# Revit family: Shower-Shower_Door-KOHLER-Levity-K-706016.rfa_
name_source: partatom
category: Specialty Equipment
units: mm (PartAtom-declared; Revit-internal decimal feet)

## family parameters
Cut with Voids When Loaded = No
Host = Face
OmniClass Number = 23.31.17.17
OmniClass Title = Shower Enclosures
Part Type = Normal
Room Calculation Point = No
Round Connector Dimension = Use Diameter
Shared = No

## types (4) — shared parameters
ADA Compliant = No
Assembly Code = C1030200
Date Modified = 07/13/2023
Default Elevation = 4"
Description = Sliding Shower Door, 74 Inch H x 44-5/8 - 47-5/8 Inch W, With 3/8 Inch Thick Crystal Clear Glass And Square Towel Bar
Hardware Included = Yes
Height = 73 9/16"
Length = 7 3/4"
Manufacturer = Kohler Co.
Master Format 2014 = 10 28 19.16
Master Format 2014 Name = Shower Doors
Material = Premium Metal Construction
Product Documentation Link = https://www.us.kohler.com
Product Name = Levity
Product Page URL = http://www.us.kohler.com
URL = https://www.us.kohler.com
WaterSense Certified = No

## per-type parameters (varying)
| type | Finish | Model | Secondary Finish | Towel Bar Finish | Type |
| ABV-Anodized Brushed Bronze | Kohler-Metal-ABV-Anodized_Brushed_Bronze | K-706016-L-ABV | Kohler-Plastic-BV-Brushed_Bronze | Kohler-Metal-BV-Brushed_Bronze | 1 |
| NX-Brushed Nickel | Kohler-Metal-NX-Brushed_Nickel | K-706016-L-NX | KOHLER-Plastic-BN-Vibrant_Brushed_Nickel | Kohler-Metal-BN-Vibrant_Brushed_Nickel | 2 |
| SHP-Bright Polished Silver | Kohler-Metal-SHP-Bright_Polished_Silver | K-706016-L-SHP | Kohler-Plastic-CP-Polished_Chrome | Kohler-Metal-CP-Polished_Chrome | 3 |
| SH-Bright Silver | Kohler-Metal-SH-Bright_Silver | K-706016-L-SH | Kohler-Plastic-CP-Polished_Chrome | Kohler-Metal-CP-Polished_Chrome | 4 |

## geometry (parser evidence)
native form markers: Sweep x5
no freeform markers — native parametric forms only
